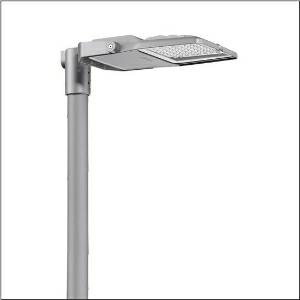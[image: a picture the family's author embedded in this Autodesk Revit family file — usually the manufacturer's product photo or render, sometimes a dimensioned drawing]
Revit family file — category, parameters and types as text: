
# Revit family: floodlight_fl_21_mini___pl61_5xa7776b4c3a_7d7f
name_source: partatom
category: Lighting Fixtures
units: mm (PartAtom-declared; Revit-internal decimal feet)

## family parameters
Cut with Voids When Loaded = No
Host = Face
Light Source = No
Part Type = Normal
Room Calculation Point = No
Round Connector Dimension = Use Diameter
Shared = No

## types (1)
- --- (1 x LED, 6360 lm, 45.7 W, 4000K)
    Apparent Load = 46 VA
    CIE Flux Codes = 33 65 98 100 100
    Color Rendering = 70
    Color Temperature = 4000K
    Default Elevation = 1800 mm
    Description = Floodlight FL 21 mini, floodlight, primary light control with lens, of PMMA, primary optical cover: protective disc, of toughened safety glass, transparent, light distribution: PL61, light emission: direct distribution, installation type: surface-mounted, LED, High Power LED, rated luminous flux: 6.360lm, luminous efficacy: 139lm/W, light colour: 740, colour temperature: 4000K, control gear: D4iSmart Interface (Zhaga), control: overheat protection, constant luminous flux control, time-dependent luminous flux control, flexible luminous flux parameterisation, pre-setting: logarithmic dimming characteristic, with terminal, 6-pole, mains connection: 220..240V, AC, 50/60Hz, start of lifetime: 46W, end of service life: 48W, reduction: 22W, mast bracket, of diecast aluminium, powder-coated, SITECO metallic grey (DB 702S), corrosivity category C5 mid according to DIN EN ISO 12944, suitable for swimming pools, chlorine-resistant, sealing non-destructively replaceable, mast bracket, of steel, galvanised, powder-coated, SITECO metallic grey (DB 702S), Smart Interface below and above, protection rating (complete): IP66, insulation class (complete): insulation class II (safety insulation), certification: CE, ENEC, VDE, protection symbol: D, impact resistance: IK08, permissible operating ambient temperature: -40..+40°C, permissible operating ambient temperature for outdoor applications: -40..+50°C, standard: DIN EN 12944, LABS conformity tested according to VDMA 24364:2018-05, packaging unit: 1 piece

Light Distribution: PL61
    Height = 70 mm
    Lamp = 1 x LED
    Lamp Light Flux = 6360 lm
    Lamp Power = 45.7 W
    Lamp count = 1
    Length = 485 mm
    Luminous efficacy = 139 lm/W
    Manufacturer = Siteco
    ModVariant = No
    Model = 5XA7776B4C3A
    Number of Poles = 1
    OnlyDefault = Yes
    Power Factor = 1
    Product Name = Floodlight FL 21 mini | PL61
    Product group = floodlight | pylon annexe
    ProductGroupID = 6201
    Protection Class = Protection class II
    Protection Degree = IP 66
    RLX_Detail_Level = 1
    RLX_Emergency_Light_Flux = 0 lm
    RLX_Emergency_Type = 0
    RLX_Emergency_Type_DB = No
    RlxData = <blob elided: 101125 chars, md5=af3df79d>
    Socket = socket
    Standby Power = 0 W
    System Light Flux = 6360 lm
    System Power = 46 W
    Type Comments = factory setting: luminous flux: 100 % | dim-lin: 254 | 463 mA
    Type Image = l_1007125.jpg
    URL = http://relux.com
    VarID = @adj_102155
    Voltage = 0 V
    Weight = 0.00 kg
    Width = 337 mm

## geometry (parser evidence)
native form markers: Blend x4, Sweep x13
no freeform markers — native parametric forms only
